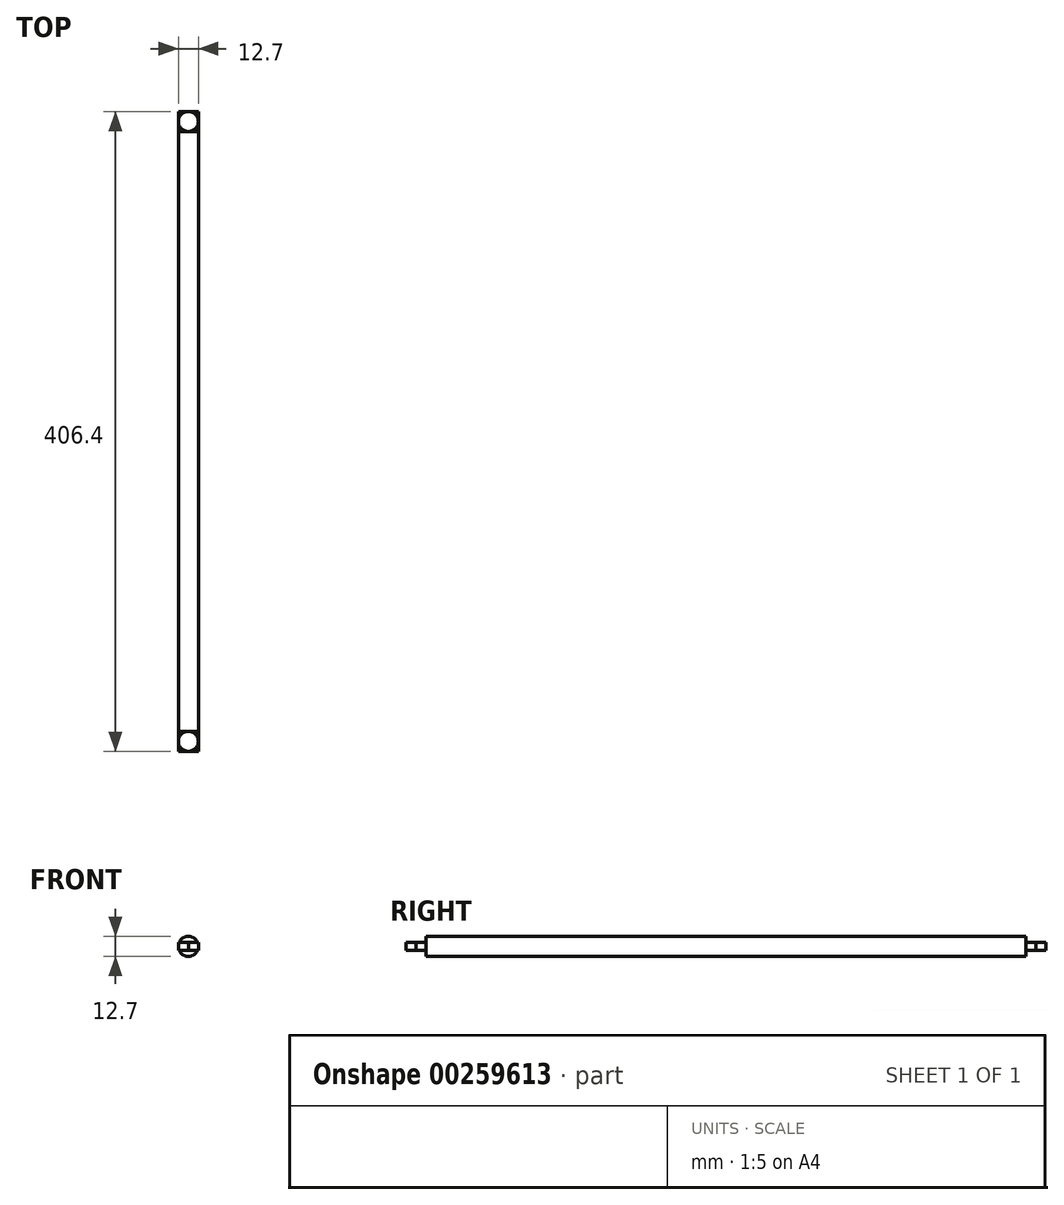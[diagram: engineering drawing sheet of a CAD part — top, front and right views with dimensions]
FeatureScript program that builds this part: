
annotation { "Feature Type Name" : "Feature", "Feature Type Description" : "" }
export const myFeature = defineFeature(function(context is Context, id is Id, definition is map)
    precondition{}
    {
        {
            var Q0;
            Q0=qCreatedBy(makeId("Front.planeOp"),FACE);
            var sketch = newSketch(context, id + "F0", { "sketchPlane" : qUnion([Q0])});
            skCircle(sketch, "E0", {"center": v(0, 0) * mm, "radius": 6.35 * mm});
            skSolve(sketch);
        }
        {
            var Q0;
            Q0=makeQuery(id+"F0.imprint","IMPRINT",FACE,{"disambiguationData":[TD([[makeQuery(id+"F0.imprint","IMPRINT",EDGE,{"derivedFrom":sQuery(id+"F0.wireOp",EDGE,"E0")}),1.0]])]});
            extrude(context, id + "F1", {"entities" : qUnion([Q0]), "depth" : 381 * mm, "symmetric" : true});
        }
        {
            var Q0;
            Q0=qCreatedBy(makeId("Top.planeOp"),FACE);
            var sketch = newSketch(context, id + "F2", { "sketchPlane" : qUnion([Q0])});
            skLineSegment(sketch, "E1.bottom", {"start": v(6.35, -203.2) * mm, "end": v(-6.35, -203.2) * mm});
            skLineSegment(sketch, "E1.top", {"start": v(6.35, -190.5) * mm, "end": v(-6.35, -190.5) * mm});
            skLineSegment(sketch, "E1.left", {"start": v(6.35, -203.2) * mm, "end": v(6.35, -190.5) * mm});
            skLineSegment(sketch, "E1.right", {"start": v(-6.35, -203.2) * mm, "end": v(-6.35, -190.5) * mm});
            skPoint(sketch, "E1.middle", {"position": v(0, -196.85) * mm});
            skLineSegment(sketch, "E2.MirrorCS", {"start": v(-6.35, 203.2) * mm, "end": v(-6.35, 190.5) * mm});
            skLineSegment(sketch, "E3.MirrorCS", {"start": v(6.35, 203.2) * mm, "end": v(-6.35, 203.2) * mm});
            skLineSegment(sketch, "E4.MirrorCS", {"start": v(6.35, 203.2) * mm, "end": v(6.35, 190.5) * mm});
            skLineSegment(sketch, "E5.MirrorCS", {"start": v(6.35, 190.5) * mm, "end": v(-6.35, 190.5) * mm});
            skSolve(sketch);
        }
        {
            var Q0;
            Q0 = qSketchRegion(id + "F2", true);
            extrude(context, id + "F3", {"entities" : qUnion([Q0]), "operationType" : NewBodyOperationType.ADD, "depth" : 5.08 * mm, "symmetric" : true});
        }
        {
            var Q0;
            Q0=makeQuery(id+"F3.opExtrude","CAP_FACE",FACE,{"disambiguationData":[OSD([sQuery(id+"F2.wireOp",EDGE,"E2.MirrorCS"),sQuery(id+"F2.wireOp",EDGE,"E3.MirrorCS"),sQuery(id+"F2.wireOp",EDGE,"E4.MirrorCS"),sQuery(id+"F2.wireOp",EDGE,"E5.MirrorCS")])],"isStart":false});
            var sketch = newSketch(context, id + "F4", { "sketchPlane" : qUnion([Q0])});
            skCircle(sketch, "E6", {"center": v(0, 196.85) * mm, "radius": 6.35 * mm});
            skPoint(sketch, "E6.centerSnap0", {"position": v(0, 203.2) * mm});
            skCircle(sketch, "E7.MirrorC", {"center": v(0, -196.85) * mm, "radius": 6.35 * mm});
            skSolve(sketch);
        }
        {
            var Q0;
            Q0 = qSketchRegion(id + "F4", true);
            extrude(context, id + "F5", {"entities" : qUnion([Q0]), "operationType" : NewBodyOperationType.REMOVE, "endBound" : BoundingType.THROUGH_ALL, "oppositeDirection" : true, "depth" : 25.4 * mm});
        }
    });
